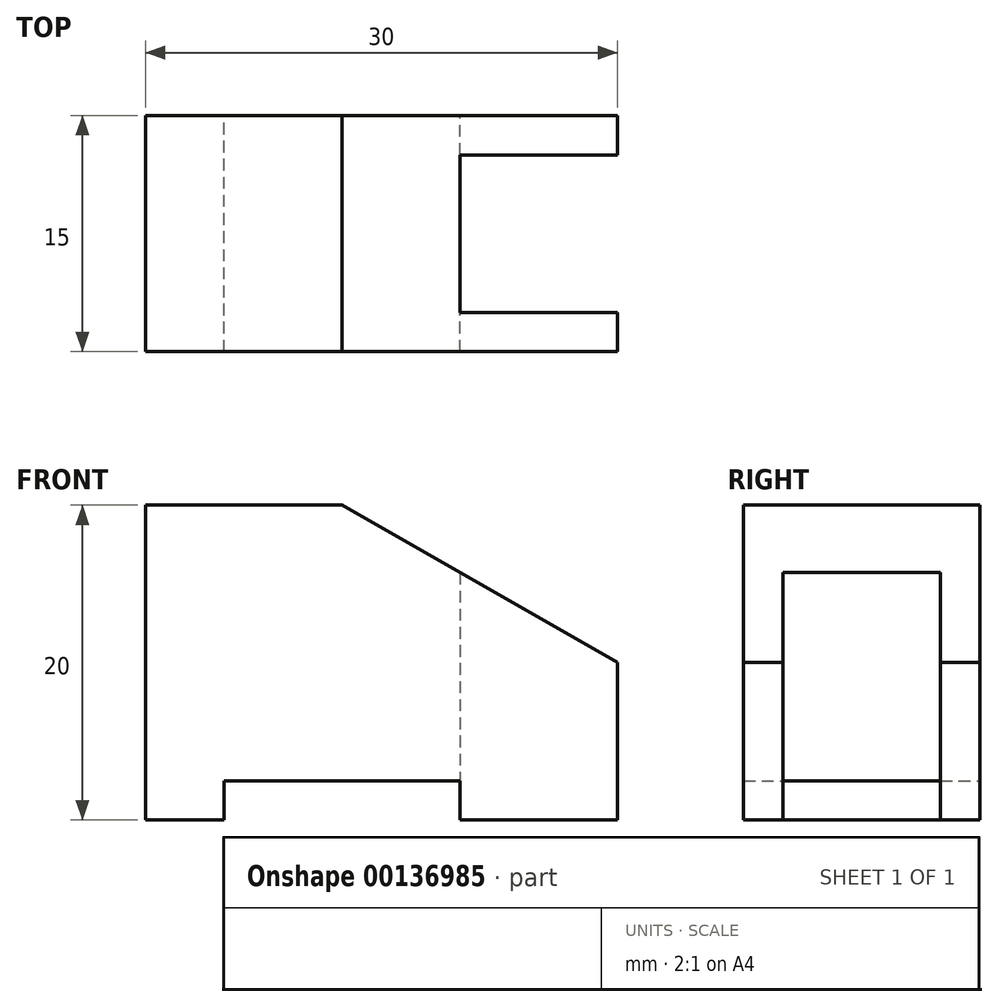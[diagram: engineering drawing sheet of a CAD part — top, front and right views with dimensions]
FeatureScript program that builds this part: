
annotation { "Feature Type Name" : "Feature", "Feature Type Description" : "" }
export const myFeature = defineFeature(function(context is Context, id is Id, definition is map)
    precondition{}
    {
        {
            var Q0;
            Q0=qCreatedBy(makeId("Front.planeOp"),FACE);
            var sketch = newSketch(context, id + "F0", { "sketchPlane" : qUnion([Q0])});
            skLineSegment(sketch, "E0", {"start": v(-15, 0) * mm, "end": v(-15, 20) * mm});
            skLineSegment(sketch, "E1", {"start": v(-15, 20) * mm, "end": v(-2.5, 20) * mm});
            skLineSegment(sketch, "E2", {"start": v(-2.5, 20) * mm, "end": v(15, 10) * mm});
            skLineSegment(sketch, "E3", {"start": v(15, 10) * mm, "end": v(15, 0) * mm});
            skLineSegment(sketch, "E4", {"start": v(15, 0) * mm, "end": v(5, 0) * mm});
            skLineSegment(sketch, "E5", {"start": v(5, 0) * mm, "end": v(5, 2.5) * mm});
            skLineSegment(sketch, "E6", {"start": v(5, 2.5) * mm, "end": v(-10, 2.5) * mm});
            skLineSegment(sketch, "E7", {"start": v(-10, 2.5) * mm, "end": v(-10, 0) * mm});
            skLineSegment(sketch, "E8", {"start": v(-10, 0) * mm, "end": v(-15, 0) * mm});
            skSolve(sketch);
        }
        {
            var Q0;
            Q0 = qSketchRegion(id + "F0", true);
            extrude(context, id + "F1", {"entities" : qUnion([Q0]), "endBound" : BoundingType.SYMMETRIC, "depth" : 15 * mm});
        }
        {
            var Q0;
            Q0=qCreatedBy(makeId("Top.planeOp"),FACE);
            var sketch = newSketch(context, id + "F2", { "sketchPlane" : qUnion([Q0])});
            skLineSegment(sketch, "E9.bottom", {"start": v(15, -5) * mm, "end": v(5, -5) * mm});
            skLineSegment(sketch, "E9.top", {"start": v(15, 5) * mm, "end": v(5, 5) * mm});
            skLineSegment(sketch, "E9.left", {"start": v(15, -5) * mm, "end": v(15, 5) * mm});
            skLineSegment(sketch, "E9.right", {"start": v(5, -5) * mm, "end": v(5, 5) * mm});
            skSolve(sketch);
        }
        {
            var Q0;
            Q0 = qSketchRegion(id + "F2", true);
            extrude(context, id + "F3", {"entities" : qUnion([Q0]), "operationType" : NewBodyOperationType.REMOVE, "endBound" : BoundingType.THROUGH_ALL, "depth" : 15 * mm});
        }
    });
